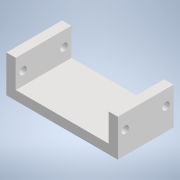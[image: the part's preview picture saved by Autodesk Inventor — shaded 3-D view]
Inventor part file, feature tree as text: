
AUTODESK INVENTOR PART (.ipt)
format: ipt  version: 2022 (Build 260153070, 153G)  size: 139,264 bytes
history: native  units: mm
features: sketch x7, hole x5, extrude x2
ambient origin geometry x8: Origin, YZ Plane, XZ Plane, XY Plane, X Axis, Y Axis, Z Axis, Center Point
bodies: Solid1 (feature_tree)
feature tree (14):
  extrude  "Extrusion1"  Depth=76.2mm
  extrude  "Extrusion2"  Depth=127.0mm
  hole  "Hole1"  [1 undecoded]
  hole  "Hole2"  [1 undecoded]
  hole  "Hole3"  [1 undecoded]
  hole  "Hole4"  [1 undecoded]
  hole  "Hole5"  [1 undecoded]
  sketch  "Sketch2"  dims[d0=152.4mm d1=76.2mm]
  sketch  "Sketch3"  dims[d2=50.8mm d3=0.0mm d4=127.0mm]
  sketch  "Sketch4"  dims[d5=76.2mm d6=38.1mm d7=0.0mm]
  sketch  "Sketch5"  dims[d8=20.32mm d9=10.16mm]
  sketch  "Sketch6"  dims[d10=10.0mm d11=6.0mm d12=3.023mm d13=2.0mm d14=14.3117mm d15=8.0mm d16=20.594885mm d17=20.32mm]
  sketch  "Sketch7"  dims[d18=10.16mm]
  sketch  "Sketch8"  dims[d19=10.0mm d20=6.0mm d21=4.0mm d22=2.0mm d23=90.0deg d24=8.0mm d25=20.594885mm d26=20.32mm d27=10.16mm d28=20.32mm d29=10.16mm d30=10.0mm d31=6.0mm d32=4.0mm d33=2.0mm d34=90.0deg d35=8.0mm d36=20.594885mm d37=20.32mm d38=37.0mm d39=10.0mm d40=6.0mm d41=4.0mm d42=2.0mm d43=90.0deg d44=8.0mm d45=20.594885mm d46=20.32mm d47=37.0mm d48=10.0mm d49=6.0mm d50=4.0mm d51=2.0mm d52=90.0deg d53=8.0mm d54=20.594885mm]
note: 5 required parameter values undecoded (feature->parameter linkage not recoverable at this tier; creation-order binding heuristic only, values carry confidence <= 0.55)
